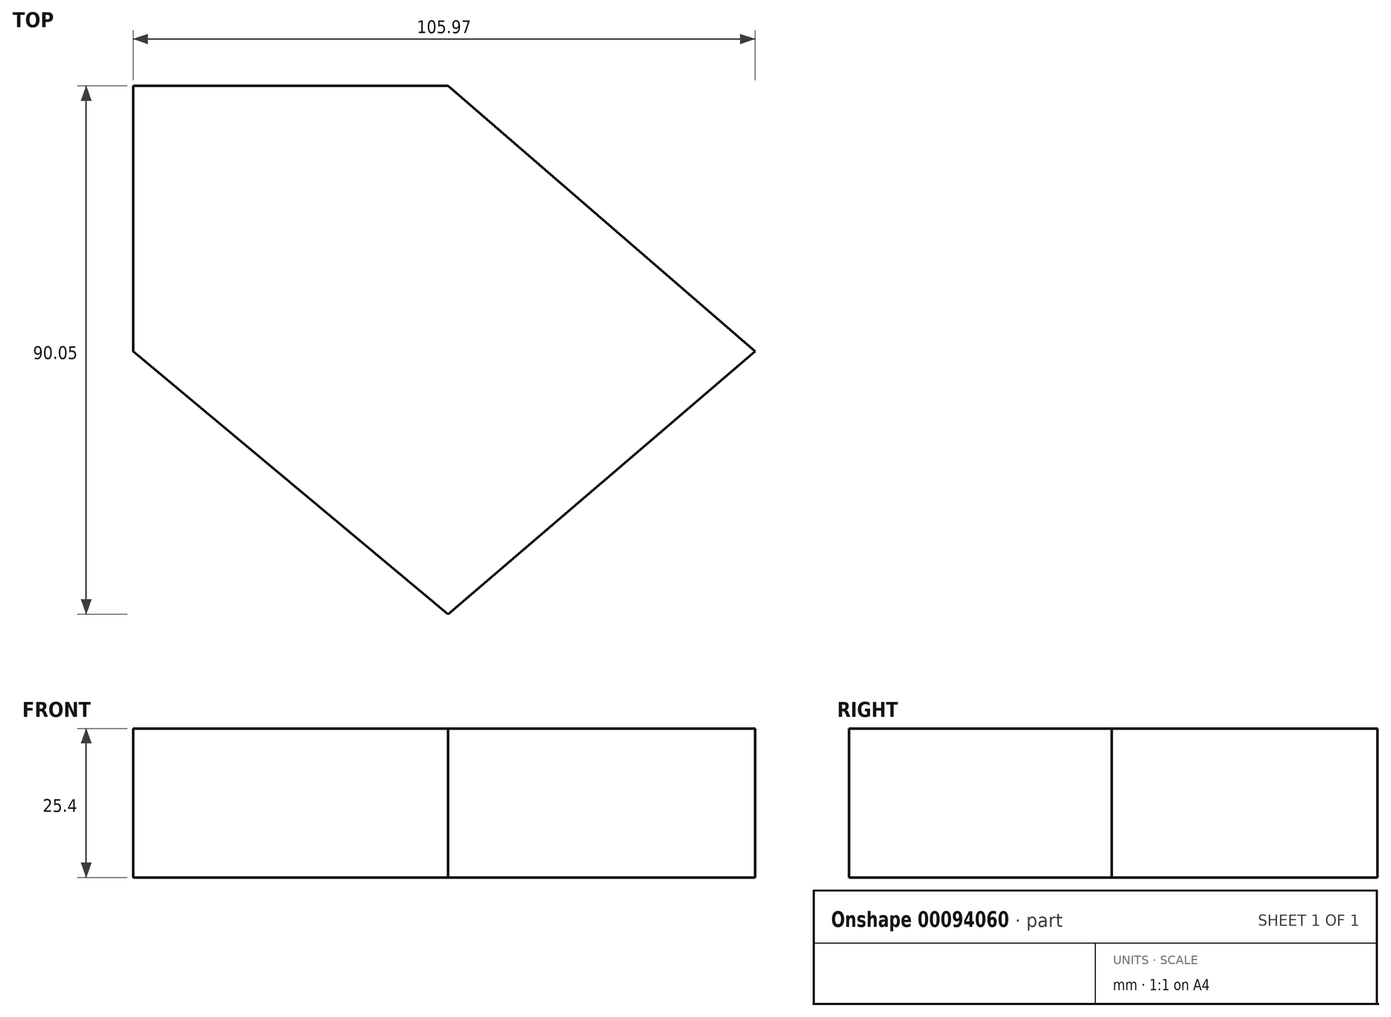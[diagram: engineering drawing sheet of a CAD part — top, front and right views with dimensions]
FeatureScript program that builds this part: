
annotation { "Feature Type Name" : "Feature", "Feature Type Description" : "" }
export const myFeature = defineFeature(function(context is Context, id is Id, definition is map)
    precondition{}
    {
        {
            var Q0;
            Q0=qCreatedBy(makeId("Top.planeOp"),FACE);
            var sketch = newSketch(context, id + "F0", { "sketchPlane" : qUnion([Q0])});
            skLineSegment(sketch, "E0", {"start": v(-53.67, 0) * mm, "end": v(-53.67, 45.25) * mm});
            skLineSegment(sketch, "E1", {"start": v(-53.67, 45.25) * mm, "end": v(0, 45.25) * mm});
            skLineSegment(sketch, "E2", {"start": v(0, 45.25) * mm, "end": v(52.3, 0) * mm});
            skLineSegment(sketch, "E3", {"start": v(52.3, 0) * mm, "end": v(0, -44.8) * mm});
            skLineSegment(sketch, "E4", {"start": v(0, -44.8) * mm, "end": v(-53.67, 0) * mm});
            skSolve(sketch);
        }
        {
            var Q0;
            Q0=makeQuery(id+"F0.imprint","IMPRINT",FACE,{"disambiguationData":[TD([[makeQuery(id+"F0.imprint","IMPRINT",EDGE,{"derivedFrom":sQuery(id+"F0.wireOp",EDGE,"E0")}),-1.0]])]});
            extrude(context, id + "F1", {"entities" : qUnion([Q0]), "depth" : 25.4 * mm});
        }
    });
